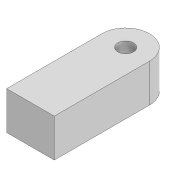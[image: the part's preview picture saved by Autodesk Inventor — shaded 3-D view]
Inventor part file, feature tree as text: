
AUTODESK INVENTOR PART (.ipt)
format: ipt  version: 2022 (Build 260153000, 153)  size: 82,944 bytes
history: native  units: mm
features: extrude x1, sketch x1
ambient origin geometry x8: Origin, YZ Plane, XZ Plane, XY Plane, X Axis, Y Axis, Z Axis, Center Point
bodies: Solid1 (feature_tree)
feature tree (2):
  extrude  "Extrusion1"  Depth=10.0mm
  sketch  "Sketch1"  dims[d0=3.3mm d1=10.0mm d2=20.0mm d3=8.0mm d4=0.0mm]
